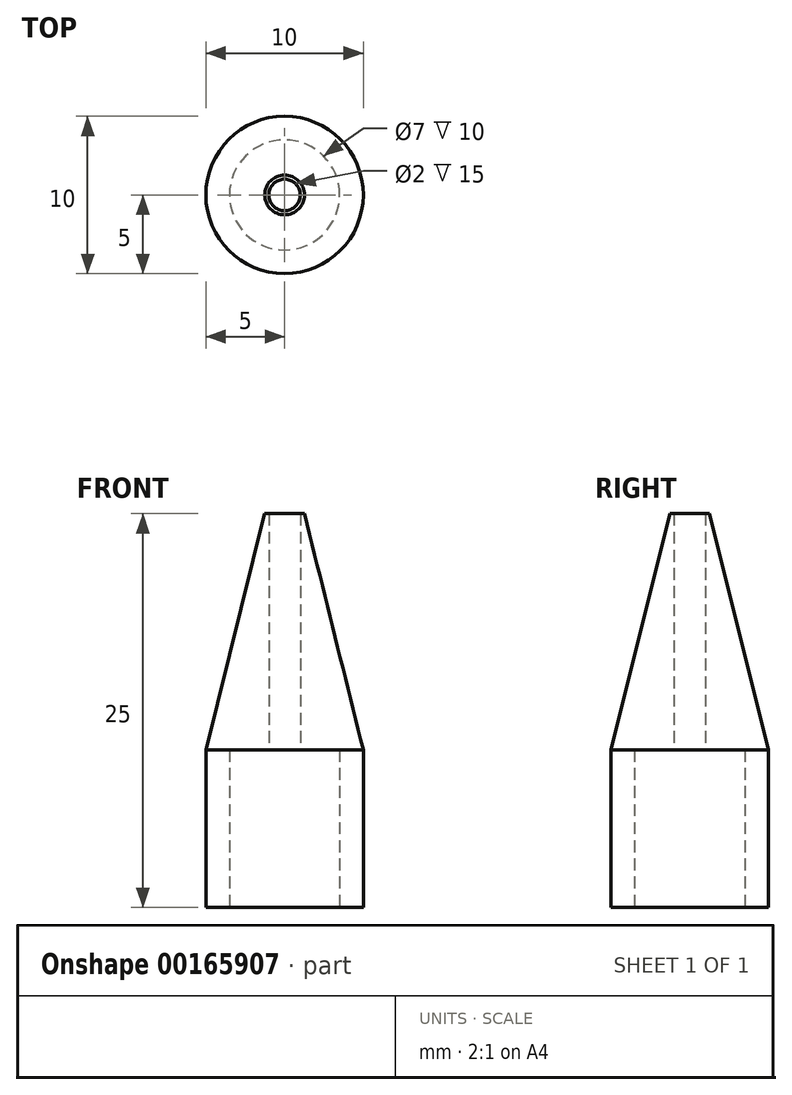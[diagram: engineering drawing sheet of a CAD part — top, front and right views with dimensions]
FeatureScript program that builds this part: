
annotation { "Feature Type Name" : "Feature", "Feature Type Description" : "" }
export const myFeature = defineFeature(function(context is Context, id is Id, definition is map)
    precondition{}
    {
        {
            var Q0;
            Q0=qCreatedBy(makeId("Top.planeOp"),FACE);
            var sketch = newSketch(context, id + "F0", { "sketchPlane" : qUnion([Q0])});
            skCircle(sketch, "E0", {"center": v(0, 0) * mm, "radius": 5 * mm});
            skCircle(sketch, "E1", {"center": v(0, 0) * mm, "radius": 1 * mm});
            skCircle(sketch, "E2", {"center": v(0, 0) * mm, "radius": 3.5 * mm});
            skSolve(sketch);
        }
        {
            var Q0;
            Q0=makeQuery(id+"F0.imprint","IMPRINT",FACE,{"disambiguationData":[TD([[makeQuery(id+"F0.imprint","IMPRINT",EDGE,{"derivedFrom":sQuery(id+"F0.wireOp",EDGE,"E0")}),1.0]])]});
            extrude(context, id + "F1", {"entities" : qUnion([Q0]), "depth" : 10 * mm});
        }
        {
            var Q0;
            Q0=makeQuery(id+"F1.opExtrude","CAP_FACE",FACE,{"disambiguationData":[OSD([sQuery(id+"F0.wireOp",EDGE,"E0")])],"isStart":false});
            var sketch = newSketch(context, id + "F2", { "sketchPlane" : qUnion([Q0])});
            skCircle(sketch, "E3", {"center": v(0, 0) * mm, "radius": 5 * mm});
            skSolve(sketch);
        }
        {
            var Q0;
            Q0 = qSketchRegion(id + "F2", true);
            extrude(context, id + "F3", {"entities" : qUnion([Q0]), "operationType" : NewBodyOperationType.ADD, "depth" : 15 * mm, "hasDraft" : true, "draftAngle" : 14 * degree, "draftPullDirection" : true});
        }
        {
            var Q0;
            Q0=makeQuery(id+"F0.imprint","IMPRINT",FACE,{"disambiguationData":[TD([[makeQuery(id+"F0.imprint","IMPRINT",EDGE,{"derivedFrom":sQuery(id+"F0.wireOp",EDGE,"E1")}),1.0]])]});
            extrude(context, id + "F4", {"entities" : qUnion([Q0]), "operationType" : NewBodyOperationType.REMOVE, "endBound" : BoundingType.THROUGH_ALL, "depth" : 25 * mm});
        }
    });
